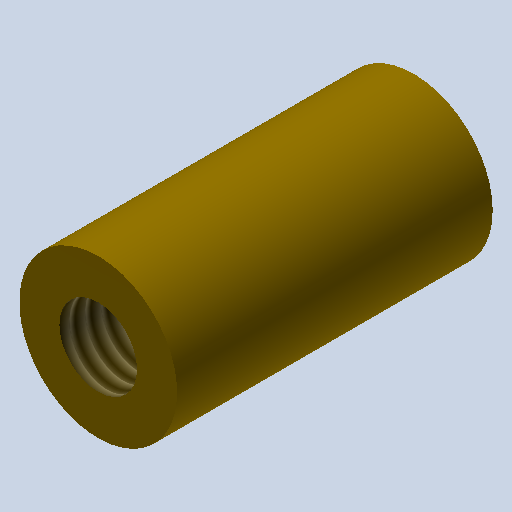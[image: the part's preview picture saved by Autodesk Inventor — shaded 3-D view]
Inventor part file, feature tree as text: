
AUTODESK INVENTOR PART (.ipt)
format: ipt  version: 2022 (Build 260153000, 153)  size: 114,688 bytes
history: native  units: mm
features: sketch x2, extrude x1, hole x1
ambient origin geometry x8: Origin, YZ Plane, XZ Plane, XY Plane, X Axis, Y Axis, Z Axis, Center Point
bodies: Solid1 (feature_tree)
feature tree (4):
  extrude  "Extrusion1"  Depth=10.0mm TaperAngle=0.0deg
  hole  "Hole1"  [1 undecoded]
  sketch  "Sketch1"  dims[d0=5.0mm d1=10.0mm d2=0.0mm]
  sketch  "Sketch2"  dims[d3=2.459mm d4=10.0mm d5=4.0mm d6=2.0mm d7=90.0deg d8=8.0mm d9=20.594885mm]
note: 1 required parameter value undecoded (feature->parameter linkage not recoverable at this tier; creation-order binding heuristic only, values carry confidence <= 0.55)
